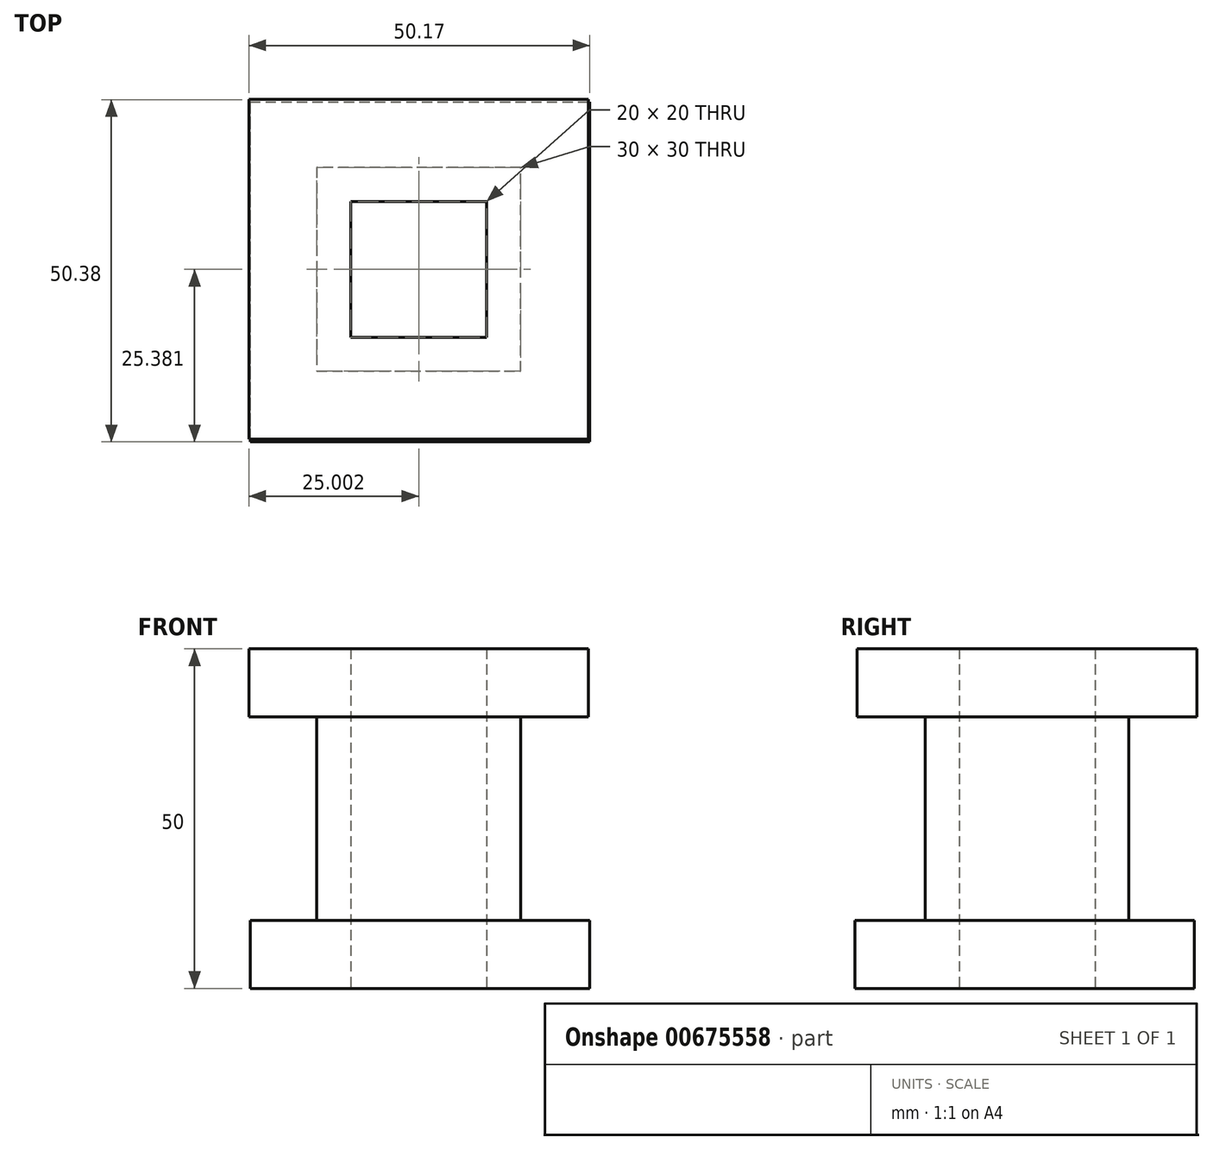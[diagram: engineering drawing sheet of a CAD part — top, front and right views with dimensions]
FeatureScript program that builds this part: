
annotation { "Feature Type Name" : "Feature", "Feature Type Description" : "" }
export const myFeature = defineFeature(function(context is Context, id is Id, definition is map)
    precondition{}
    {
        {
            var Q0;
            Q0=qCreatedBy(makeId("Top.planeOp"),FACE);
            var sketch = newSketch(context, id + "F0", { "sketchPlane" : qUnion([Q0])});
            skLineSegment(sketch, "E0", {"start": v(-46.77, 35.36) * mm, "end": v(-46.77, -14.64) * mm});
            skLineSegment(sketch, "E1", {"start": v(-46.77, 35.36) * mm, "end": v(3.23, 35.36) * mm});
            skLineSegment(sketch, "E2", {"start": v(3.23, 35.36) * mm, "end": v(3.23, -14.64) * mm});
            skLineSegment(sketch, "E3", {"start": v(-46.77, -14.64) * mm, "end": v(3.23, -14.64) * mm});
            skLineSegment(sketch, "E4", {"start": v(-31.77, 20.36) * mm, "end": v(-31.77, 0.36) * mm});
            skLineSegment(sketch, "E5", {"start": v(-31.77, 0.36) * mm, "end": v(-11.77, 0.36) * mm});
            skLineSegment(sketch, "E6", {"start": v(-11.77, 0.36) * mm, "end": v(-11.77, 20.36) * mm});
            skLineSegment(sketch, "E7", {"start": v(-11.77, 20.36) * mm, "end": v(-31.77, 20.36) * mm});
            skSolve(sketch);
        }
        {
            var Q0;
            Q0 = qSketchRegion(id + "F0", true);
            extrude(context, id + "F1", {"entities" : qUnion([Q0]), "depth" : 10 * mm, "offsetDistance" : 25 * mm});
        }
        {
            var Q0;
            Q0=makeQuery(id+"F1.opExtrude","CAP_FACE",FACE,{"disambiguationData":[OSD([sQuery(id+"F0.wireOp",EDGE,"E0"),sQuery(id+"F0.wireOp",EDGE,"E1"),sQuery(id+"F0.wireOp",EDGE,"E2"),sQuery(id+"F0.wireOp",EDGE,"E3"),sQuery(id+"F0.wireOp",EDGE,"E4"),sQuery(id+"F0.wireOp",EDGE,"E5"),sQuery(id+"F0.wireOp",EDGE,"E6"),sQuery(id+"F0.wireOp",EDGE,"E7")])],"isStart":true});
            var sketch = newSketch(context, id + "F2", { "sketchPlane" : qUnion([Q0])});
            skLineSegment(sketch, "E8", {"start": v(-31.77, -0.36) * mm, "end": v(-11.77, -0.36) * mm});
            skLineSegment(sketch, "E9", {"start": v(-11.77, -0.36) * mm, "end": v(-11.77, -20.36) * mm});
            skLineSegment(sketch, "E10", {"start": v(-11.77, -20.36) * mm, "end": v(-31.77, -20.36) * mm});
            skLineSegment(sketch, "E11", {"start": v(-31.77, -20.36) * mm, "end": v(-31.77, -0.36) * mm});
            skLineSegment(sketch, "E12", {"start": v(-36.77, 4.64) * mm, "end": v(-6.77, 4.64) * mm});
            skLineSegment(sketch, "E13", {"start": v(-6.77, 4.64) * mm, "end": v(-6.77, -25.36) * mm});
            skLineSegment(sketch, "E14", {"start": v(-6.77, -25.36) * mm, "end": v(-36.77, -25.36) * mm});
            skLineSegment(sketch, "E15", {"start": v(-36.77, -25.36) * mm, "end": v(-36.77, 4.64) * mm});
            skSolve(sketch);
        }
        {
            var Q0;
            Q0 = qSketchRegion(id + "F2", true);
            extrude(context, id + "F3", {"entities" : qUnion([Q0]), "operationType" : NewBodyOperationType.ADD, "depth" : 30 * mm, "offsetDistance" : 25 * mm});
        }
        {
            var Q0;
            Q0=makeQuery(id+"F3.opExtrude","CAP_FACE",FACE,{"disambiguationData":[OSD([sQuery(id+"F2.wireOp",EDGE,"E8"),sQuery(id+"F2.wireOp",EDGE,"E9"),sQuery(id+"F2.wireOp",EDGE,"E10"),sQuery(id+"F2.wireOp",EDGE,"E11"),sQuery(id+"F2.wireOp",EDGE,"E12"),sQuery(id+"F2.wireOp",EDGE,"E13"),sQuery(id+"F2.wireOp",EDGE,"E14"),sQuery(id+"F2.wireOp",EDGE,"E15")])],"isStart":false});
            var sketch = newSketch(context, id + "F4", { "sketchPlane" : qUnion([Q0])});
            skLineSegment(sketch, "E16", {"start": v(-31.77, -0.36) * mm, "end": v(-11.77, -0.36) * mm});
            skLineSegment(sketch, "E17", {"start": v(-11.77, -0.36) * mm, "end": v(-11.77, -20.36) * mm});
            skLineSegment(sketch, "E18", {"start": v(-11.77, -20.36) * mm, "end": v(-31.77, -20.36) * mm});
            skLineSegment(sketch, "E19", {"start": v(-31.77, -20.36) * mm, "end": v(-31.77, -0.36) * mm});
            skLineSegment(sketch, "E20", {"start": v(-46.6, 15.02) * mm, "end": v(3.4, 15.02) * mm});
            skLineSegment(sketch, "E21", {"start": v(3.4, 15.02) * mm, "end": v(3.4, -34.98) * mm});
            skLineSegment(sketch, "E22", {"start": v(-46.6, 15.02) * mm, "end": v(-46.6, -34.98) * mm});
            skLineSegment(sketch, "E23", {"start": v(-46.6, -34.98) * mm, "end": v(3.4, -34.98) * mm});
            skSolve(sketch);
        }
        {
            var Q0;
            Q0 = qSketchRegion(id + "F4", true);
            extrude(context, id + "F5", {"entities" : qUnion([Q0]), "operationType" : NewBodyOperationType.ADD, "depth" : 10 * mm, "offsetDistance" : 25 * mm});
        }
    });
